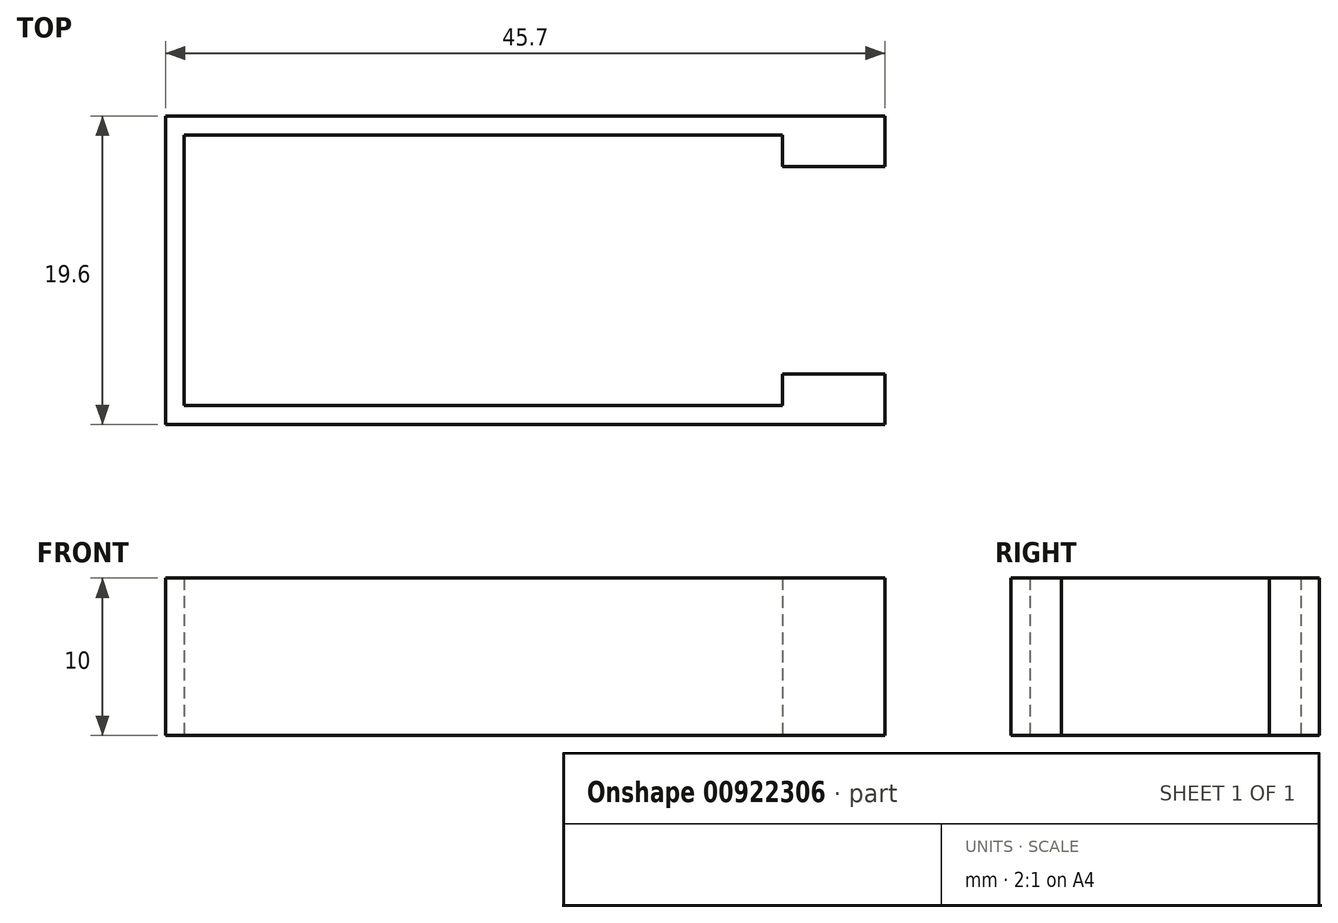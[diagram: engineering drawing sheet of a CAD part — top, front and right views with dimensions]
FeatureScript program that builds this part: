
annotation { "Feature Type Name" : "Feature", "Feature Type Description" : "" }
export const myFeature = defineFeature(function(context is Context, id is Id, definition is map)
    precondition{}
    {
        {
            var Q0;
            Q0=qCreatedBy(makeId("Top.planeOp"),FACE);
            var sketch = newSketch(context, id + "F0", { "sketchPlane" : qUnion([Q0])});
            skLineSegment(sketch, "E0.bottom", {"start": v(0, 0) * mm, "end": v(-6.5, 0) * mm});
            skLineSegment(sketch, "E0.top", {"start": v(0, 6.6) * mm, "end": v(-6.5, 6.6) * mm});
            skLineSegment(sketch, "E0.left", {"start": v(0, 0) * mm, "end": v(0, 6.6) * mm});
            skLineSegment(sketch, "E0.right", {"start": v(-6.5, 0) * mm, "end": v(-6.5, 6.6) * mm});
            skLineSegment(sketch, "E1", {"start": v(-6.5, 6.6) * mm, "end": v(-6.5, 8.6) * mm});
            skLineSegment(sketch, "E2", {"start": v(-6.5, 8.6) * mm, "end": v(-44.5, 8.6) * mm});
            skLineSegment(sketch, "E3", {"start": v(-44.5, 8.6) * mm, "end": v(-44.5, 0) * mm});
            skLineSegment(sketch, "E4", {"start": v(-44.5, 0) * mm, "end": v(-6.5, 0) * mm});
            skLineSegment(sketch, "E5", {"start": v(-6.5, 8.6) * mm, "end": v(0, 8.6) * mm});
            skLineSegment(sketch, "E6", {"start": v(0, 8.6) * mm, "end": v(0, 6.6) * mm});
            skLineSegment(sketch, "E7.0", {"start": v(-45.7, 9.8) * mm, "end": v(-45.7, 0) * mm});
            skLineSegment(sketch, "E7.1", {"start": v(-5.5, 9.8) * mm, "end": v(-45.7, 9.8) * mm});
            skLineSegment(sketch, "E8.0", {"start": v(-5.5, 9.8) * mm, "end": v(0, 9.8) * mm});
            skLineSegment(sketch, "E9", {"start": v(0, 9.8) * mm, "end": v(0, 8.6) * mm});
            skLineSegment(sketch, "E10.MirrorCS", {"start": v(-6.5, -8.6) * mm, "end": v(-44.5, -8.6) * mm});
            skLineSegment(sketch, "E11.MirrorCS", {"start": v(-44.5, -8.6) * mm, "end": v(-44.5, 0) * mm});
            skLineSegment(sketch, "E12.MirrorCS", {"start": v(-45.7, -9.8) * mm, "end": v(-45.7, 0) * mm});
            skLineSegment(sketch, "E13.MirrorCS", {"start": v(-5.5, -9.8) * mm, "end": v(-45.7, -9.8) * mm});
            skLineSegment(sketch, "E14.MirrorCS", {"start": v(-5.5, -9.8) * mm, "end": v(0, -9.8) * mm});
            skLineSegment(sketch, "E15.MirrorCS", {"start": v(-6.5, -6.6) * mm, "end": v(-6.5, -8.6) * mm});
            skLineSegment(sketch, "E16.MirrorCS", {"start": v(0, -6.6) * mm, "end": v(-6.5, -6.6) * mm});
            skLineSegment(sketch, "E17.MirrorCS", {"start": v(0, -8.6) * mm, "end": v(0, -6.6) * mm});
            skLineSegment(sketch, "E18.MirrorCS", {"start": v(0, -9.8) * mm, "end": v(0, -8.6) * mm});
            skSolve(sketch);
        }
        {
            var Q0;
            Q0=makeQuery(id+"F0.imprint","IMPRINT",FACE,{"disambiguationData":[TD([[makeQuery(id+"F0.imprint","IMPRINT",EDGE,{"derivedFrom":sQuery(id+"F0.wireOp",EDGE,"E2")}),-1.0]])]});
            var Q1;
            Q1=makeQuery(id+"F0.imprint","IMPRINT",FACE,{"disambiguationData":[TD([[makeQuery(id+"F0.imprint","IMPRINT",EDGE,{"derivedFrom":sQuery(id+"F0.wireOp",EDGE,"E0.top")}),-1.0]])]});
            extrude(context, id + "F1", {"entities" : qUnion([Q0, Q1]), "depth" : 10 * mm, "offsetDistance" : 25 * mm});
        }
    });
